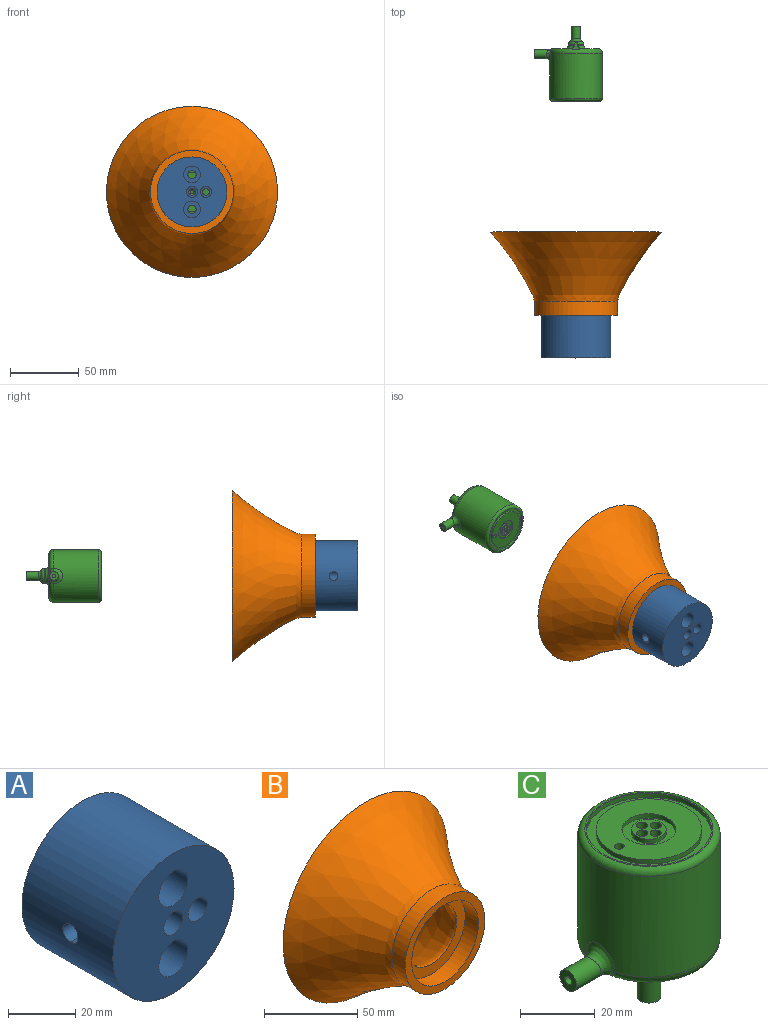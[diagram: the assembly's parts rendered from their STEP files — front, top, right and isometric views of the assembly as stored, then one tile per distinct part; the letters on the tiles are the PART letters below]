
ASSEMBLY  parts=3 mates=2
PART A: 41 faces, bbox 52.5x38.1x52.5 mm
  f0: cylinder r=4.02mm len=20.4mm, axis (0,-1,0), area 482.2mm2, adj f4,f12,f13,f14,f15,f30
  f1: cylinder r=4.02mm len=20.4mm, axis (0,-1,0), area 482.9mm2, adj f4,f10,f11,f28
  f2: plane 50.81x50.81mm, normal (0,1,0), area 475.3mm2, adj f5,f6,f8,f9,f16,f17,f18,f19
  f3: cylinder r=19.05mm len=38.1mm, axis (0,1,0), area 1140.1mm2, adj f5,f6,f7,f8,f9,f17,f18,f19
  f4: plane 50.8x50.8mm, normal (0,-1,0), area 1692mm2, adj f0,f1,f16,f23,f25
  f5: torus R=22.23mm, axis (0,1,0), area 127mm2, adj f2,f3,f17,f20
  f6: torus R=22.23mm, axis (0,1,0), area 127mm2, adj f2,f3,f18,f19
  f7: plane 38.1x38.1mm, normal (0,1,0), area 1047.9mm2, adj f3,f21,f22,f31,f32
  f8: torus R=22.23mm, axis (0,1,0), area 127mm2, adj f2,f3,f19,f20
  f9: torus R=22.23mm, axis (0,1,0), area 127mm2, adj f2,f3,f17,f18
  f10: cylinder r=3.17mm len=22.74mm, axis (1,0,0), area 226.8mm2, adj f1,f11,f16
  f11: cylinder r=3.17mm len=22.74mm, axis (1,0,0), area 219mm2, adj f1,f10,f16,f27
  f12: plane 1.26x0.06mm, normal (1,0,0), area 0.1mm2, adj f0,f13,f15
  f13: cylinder r=3.17mm len=12.5mm, axis (1,0,0), area 117.2mm2, adj f0,f12,f14,f15,f16
  f14: plane 1.26x0.06mm, normal (1,0,0), area 0.1mm2, adj f0,f13,f15
  f15: cylinder r=3.17mm len=12.5mm, axis (1,0,0), area 117mm2, adj f0,f12,f13,f14,f16,f29
  f16: cylinder r=25.4mm len=50.8mm, axis (0,1,0), area 6017mm2, adj f2,f4,f10,f11,f13,f15
  f17: revolved ~7.41x3.44mm, area 31.2mm2, adj f2,f3,f5,f9
  f18: revolved ~7.41x3.44mm, area 31.2mm2, adj f2,f3,f6,f9
  f19: revolved ~7.41x3.44mm, area 31.2mm2, adj f2,f3,f6,f8
  f20: revolved ~7.41x3.44mm, area 31.2mm2, adj f2,f3,f5,f8
  f21: cylinder r=2.38mm len=5mm, axis (0,1,0), area 74.8mm2, adj f7,f28
  f22: cylinder r=2.38mm len=5mm, axis (0,1,0), area 74.8mm2, adj f7,f30
  f23: cylinder r=6.1mm len=24.4mm, axis (0,-1,0), area 934.6mm2, adj f4,f24
  f24: plane 12.19x12.19mm, normal (0,-1,0), area 88.5mm2, adj f23,f32
  f25: cylinder r=6.1mm len=24.4mm, axis (0,-1,0), area 934.6mm2, adj f4,f26
  f26: plane 12.19x12.19mm, normal (0,-1,0), area 88.5mm2, adj f25,f31
  f27: cylinder r=4.02mm len=3.59mm, axis (0,1,0), area 0mm2, adj f11,f28
  f28: plane 8.03x8.03mm, normal (0,-1,0), area 32.9mm2, adj f1,f21,f27
  f29: cylinder r=4.02mm len=3.59mm, axis (0,1,0), area 0mm2, adj f15,f30
  f30: plane 8.03x8.03mm, normal (0,-1,0), area 32.9mm2, adj f0,f22,f29
  f31: cylinder r=3mm len=6mm, axis (0,1,0), area 18.8mm2, adj f7,f26
  f32: cylinder r=3mm len=6mm, axis (0,1,0), area 18.8mm2, adj f7,f24
  f33: plane 8.03x8.03mm, normal (0,1,0), area 1.2mm2, adj f34,f36
  f34: cylinder r=3.97mm len=7.94mm, axis (0,-1,0), area 3.1mm2, adj f33,f35
  f35: plane 8.03x8.03mm, normal (0,-1,0), area 1.2mm2, adj f34,f36
  f36: cylinder r=4.02mm len=8.03mm, axis (0,-1,0), area 3.2mm2, adj f33,f35
  f37: plane 8.03x8.03mm, normal (0,1,0), area 1.2mm2, adj f38,f40
  f38: cylinder r=3.97mm len=7.94mm, axis (0,-1,0), area 3.1mm2, adj f37,f39
  f39: plane 8.03x8.03mm, normal (0,-1,0), area 1.2mm2, adj f38,f40
  f40: cylinder r=4.02mm len=8.03mm, axis (0,-1,0), area 3.2mm2, adj f37,f39
PART B: 7 faces, bbox 124.4x60.4x124.4 mm
  f0: revolved ~101.6x101.6mm, area 12524.1mm2, adj f1,f5
  f1: plane 124.43x124.43mm, normal (0,1,0), area 4053.7mm2, adj f0,f2
  f2: revolved ~124.43x124.43mm, area 16842mm2, adj f1,f3
  f3: cylinder r=30.2mm len=60.4mm, axis (0,-1,0), area 1897.6mm2, adj f2,f4
  f4: plane 60.4x60.4mm, normal (0,-1,0), area 854.4mm2, adj f3,f6
  f5: plane 50.6x50.6mm, normal (0,-1,0), area 902.6mm2, adj f0,f6
  f6: cylinder r=25.3mm len=50.6mm, axis (0,-1,0), area 1589.7mm2, adj f4,f5
PART C: 51 faces, bbox 51.1x41.2x54.6 mm
  f0: cylinder r=6.1mm len=37.93mm, axis (0,0,1), area 1296.3mm2, adj f21,f22,f23,f24,f25,f26,f27,f28
  f1: cylinder r=6.1mm len=37.93mm, axis (0,0,1), area 1296.3mm2, adj f21,f22,f23,f24,f25,f26,f27,f28
  f2: cylinder r=1.27mm len=20.83mm, axis (-1,0,0), area 159.7mm2, adj f10,f40,f41
  f3: cylinder r=3.17mm len=10.58mm, axis (-1,0,0), area 187.3mm2, adj f41,f43,f46,f47,f48
  f4: torus R=5.71mm, axis (0,0,1), area 58.4mm2, adj f5,f22
  f5: cylinder r=3.17mm len=8.89mm, axis (0,0,1), area 177.4mm2, adj f4,f39
  f6: torus R=1.27mm, axis (0,0,1), area 56.3mm2, adj f7,f9
  f7: torus R=3.81mm, axis (0,0,-1), area 28.6mm2, adj f6,f8
  f8: cylinder r=1.27mm len=13.97mm, axis (0,0,1), area 111.5mm2, adj f7,f39
  f9: cylinder r=3.81mm len=23.54mm, axis (0,0,1), area 563.5mm2, adj f6,f33,f34,f35,f36,f38
  f10: cylinder r=1.27mm len=34.29mm, axis (0,0,1), area 268.6mm2, adj f2,f31
  f11: torus R=17.14mm, axis (0,0,1), area 345.2mm2, adj f20,f29
  f12: cylinder r=1.49mm len=12.7mm, axis (0,0,1), area 118.6mm2, adj f36,f37,f38
  f13: cylinder r=1.49mm len=12.7mm, axis (0,0,1), area 118.6mm2, adj f35,f37,f38
  f14: cylinder r=1.49mm len=12.7mm, axis (0,0,1), area 118.6mm2, adj f34,f37,f38
  f15: cylinder r=1.49mm len=12.7mm, axis (0,0,1), area 118.6mm2, adj f33,f37,f38
  f16: cylinder r=7.21mm len=14.43mm, axis (0,0,1), area 63.3mm2, adj f31,f32
  f17: cylinder r=4.6mm len=9.2mm, axis (0,0,1), area 40.4mm2, adj f32,f37
  f18: cylinder r=16.74mm len=33.48mm, axis (0,0,1), area 146.9mm2, adj f29,f30
  f19: cylinder r=14.12mm len=28.25mm, axis (0,0,1), area 124mm2, adj f30,f31
  f20: cylinder r=19.05mm len=38.1mm, axis (0,0,1), area 3890.5mm2, adj f11,f21,f48
  f21: torus R=15.88mm, axis (0,0,1), area 501.5mm2, adj f0,f1,f20,f25,f28,f42,f46,f47
  f22: torus R=3.05mm, axis (0,0,1), area 79.7mm2, adj f0,f1,f4,f24,f26
  f23: torus R=8.13mm, axis (0,0,1), area 61.4mm2, adj f0,f1,f24,f28
  f24: cylinder r=5.59mm len=10.91mm, axis (0,0,1), area 11.4mm2, adj f0,f1,f22,f23
  f25: plane 30.24x12.99mm, normal (0,0,-1), area 205mm2, adj f0,f1,f21,f27,f42
  f26: cylinder r=5.59mm len=10.91mm, axis (0,0,1), area 11.4mm2, adj f0,f1,f22,f27
  f27: torus R=8.13mm, axis (0,0,1), area 61.4mm2, adj f0,f1,f25,f26
  f28: plane 30.23x11.71mm, normal (0,0,-1), area 202.6mm2, adj f0,f1,f21,f23
  f29: plane 34.29x34.29mm, normal (0,0,1), area 43.3mm2, adj f11,f18
  f30: plane 33.48x33.48mm, normal (0,0,1), area 253.6mm2, adj f18,f19
  f31: plane 28.25x28.25mm, normal (0,0,1), area 458mm2, adj f10,f16,f19
  f32: plane 14.43x14.43mm, normal (0,0,1), area 97.1mm2, adj f16,f17
  f33: plane 1.88x0.33mm, normal (0,0,1), area 0.3mm2, adj f9,f15
  f34: plane 1.88x0.33mm, normal (0,0,1), area 0.3mm2, adj f9,f14
  f35: plane 1.88x0.33mm, normal (0,0,1), area 0.3mm2, adj f9,f13
  f36: plane 1.88x0.33mm, normal (0,0,1), area 0.3mm2, adj f9,f12
  f37: plane 9.2x9.2mm, normal (0,0,1), area 38.7mm2, adj f12,f13,f14,f15,f17
  f38: plane 7.39x7.39mm, normal (0,0,-1), area 19mm2, adj f9,f12,f13,f14,f15
  f39: plane 6.35x6.35mm, normal (0,0,-1), area 26.6mm2, adj f5,f8
  f40: plane 2.54x2.54mm, normal (-1,0,0), area 5.1mm2, adj f2
  f41: plane 6.35x6.35mm, normal (-1,0,0), area 26.6mm2, adj f2,f3
  f42: bspline ~6.12x2.87mm, area 12.6mm2, adj f21,f25,f43,f44,f45
  f43: bspline ~4.14x1.61mm, area 5.6mm2, adj f3,f42,f44,f45
  f44: bspline ~2.19x1.17mm, area 0.5mm2, adj f42,f43,f46
  f45: bspline ~2.19x1.17mm, area 0.5mm2, adj f42,f43,f47
  f46: bspline ~3.8x3.62mm, area 10.4mm2, adj f3,f21,f44,f48
  f47: bspline ~3.78x3.6mm, area 10.4mm2, adj f3,f21,f45,f48
  f48: bspline ~10.91x6.99mm, area 62.8mm2, adj f3,f20,f46,f47
  f49: plane 12.19x12.19mm, normal (0,0,-1), area 116.7mm2, adj f1
  f50: plane 12.19x12.19mm, normal (0,0,-1), area 116.7mm2, adj f0
PLACE A t=(-34.21,-49.23,-63.85)mm
PLACE B t=(-34.21,-46.23,-63.85)mm
PLACE C rot(axis=(1,0,0),90deg) t=(-34.21,99.34,-63.85)mm
MATE slider C.f4 <-> A.f3  axis (0,-1,0) through (-34.21,99.34,-63.85)mm
MATE slider B.f3 <-> A.f3  axis (0,-1,0) through (-34.21,-46.23,-63.85)mm
